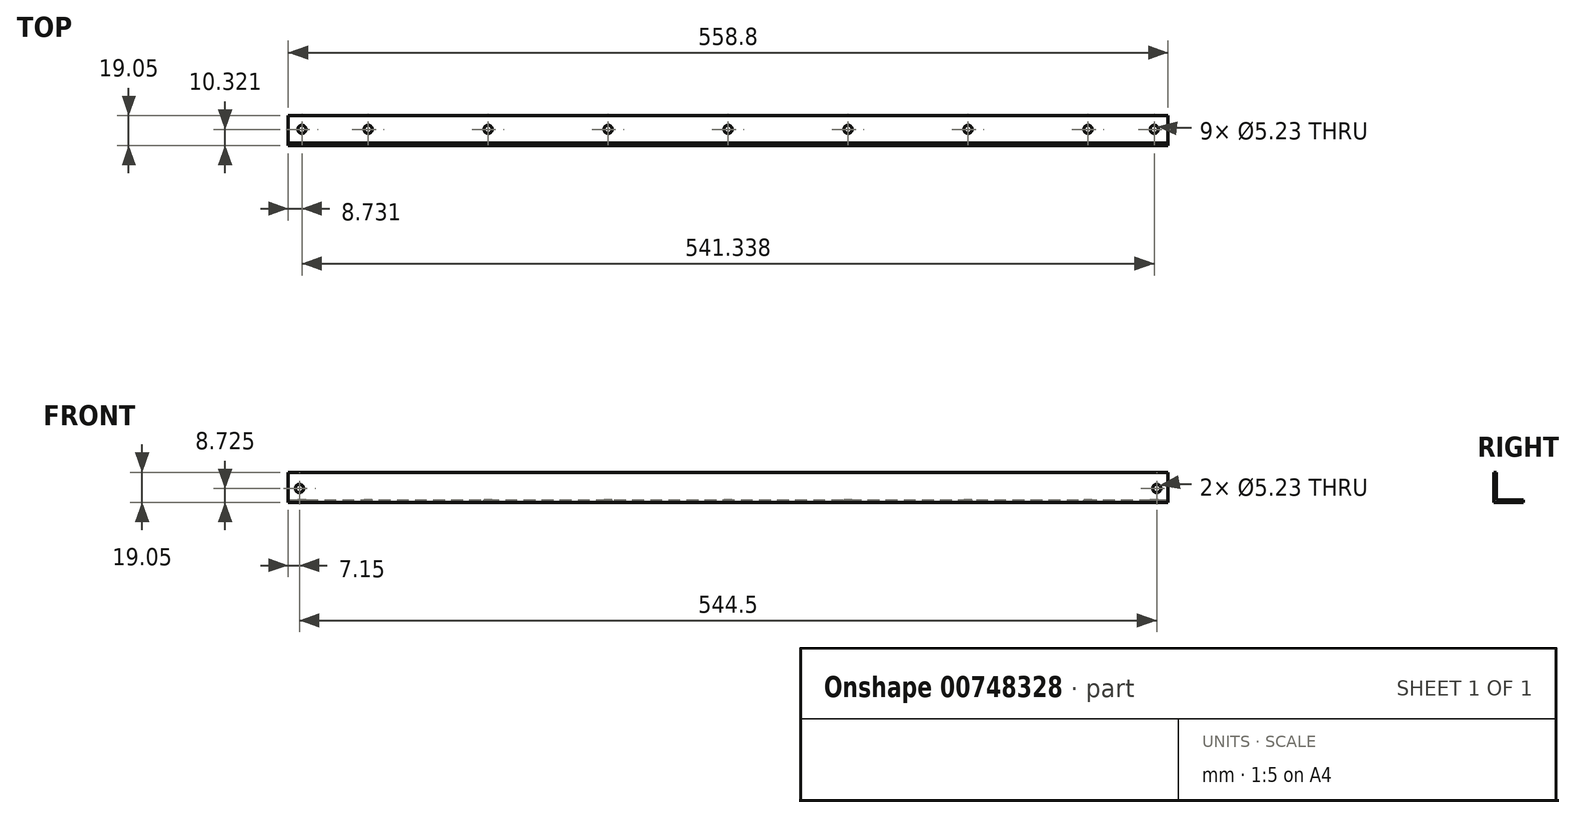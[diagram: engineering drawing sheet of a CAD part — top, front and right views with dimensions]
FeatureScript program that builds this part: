
annotation { "Feature Type Name" : "Feature", "Feature Type Description" : "" }
export const myFeature = defineFeature(function(context is Context, id is Id, definition is map)
    precondition{}
    {
        {
            var Q0;
            Q0=qCreatedBy(makeId("Right.planeOp"),FACE);
            var sketch = newSketch(context, id + "F0", { "sketchPlane" : qUnion([Q0])});
            skLineSegment(sketch, "E0", {"start": v(0, 0) * mm, "end": v(0, -17.46) * mm});
            skLineSegment(sketch, "E1", {"start": v(0, -17.46) * mm, "end": v(17.46, -17.46) * mm});
            skLineSegment(sketch, "E2.0", {"start": v(-1.59, -19.05) * mm, "end": v(17.46, -19.05) * mm});
            skLineSegment(sketch, "E2.1", {"start": v(-1.59, 0) * mm, "end": v(-1.59, -19.05) * mm});
            skLineSegment(sketch, "E3", {"start": v(-1.59, 0) * mm, "end": v(0, 0) * mm});
            skLineSegment(sketch, "E4", {"start": v(17.46, -17.46) * mm, "end": v(17.46, -19.05) * mm});
            skSolve(sketch);
        }
        {
            var Q0;
            Q0=makeQuery(id+"F0.imprint","IMPRINT",FACE,{"disambiguationData":[TD([[makeQuery(id+"F0.imprint","IMPRINT",EDGE,{"derivedFrom":sQuery(id+"F0.wireOp",EDGE,"E0")}),-1.0]])]});
            extrude(context, id + "F1", {"entities" : qUnion([Q0]), "oppositeDirection" : true, "depth" : 558.8 * mm, "offsetDistance" : 25.4 * mm});
        }
        {
            var Q0;
            Q0=makeQuery(id+"F1.opExtrude","SWEPT_FACE",FACE,{"disambiguationData":[OSD([sQuery(id+"F0.wireOp",EDGE,"E0")])]});
            var sketch = newSketch(context, id + "F2", { "sketchPlane" : qUnion([Q0])});
            skLineSegment(sketch, "E5.bottom", {"start": v(0, 0) * mm, "end": v(7.15, 0) * mm, "construction": true});
            skLineSegment(sketch, "E5.top", {"start": v(0, -17.46) * mm, "end": v(7.15, -17.46) * mm, "construction": true});
            skLineSegment(sketch, "E5.left", {"start": v(0, 0) * mm, "end": v(0, -17.46) * mm, "construction": true});
            skLineSegment(sketch, "E5.right", {"start": v(7.15, 0) * mm, "end": v(7.15, -17.46) * mm, "construction": true});
            skLineSegment(sketch, "E6.bottom", {"start": v(558.8, 0) * mm, "end": v(551.65, 0) * mm, "construction": true});
            skLineSegment(sketch, "E6.top", {"start": v(558.8, -17.46) * mm, "end": v(551.65, -17.46) * mm, "construction": true});
            skLineSegment(sketch, "E6.left", {"start": v(558.8, 0) * mm, "end": v(558.8, -17.46) * mm, "construction": true});
            skLineSegment(sketch, "E6.right", {"start": v(551.65, 0) * mm, "end": v(551.65, -17.46) * mm, "construction": true});
            skLineSegment(sketch, "E7.bottom", {"start": v(7.15, 0) * mm, "end": v(551.65, 0) * mm, "construction": true});
            skLineSegment(sketch, "E7.top", {"start": v(7.15, -17.46) * mm, "end": v(551.65, -17.46) * mm, "construction": true});
            skLineSegment(sketch, "E8.bottom", {"start": v(7.15, 0) * mm, "end": v(279.4, 0) * mm, "construction": true});
            skLineSegment(sketch, "E8.top", {"start": v(7.15, -17.46) * mm, "end": v(279.4, -17.46) * mm, "construction": true});
            skLineSegment(sketch, "E8.right", {"start": v(279.4, 0) * mm, "end": v(279.4, -17.46) * mm, "construction": true});
            skLineSegment(sketch, "E9.bottom", {"start": v(279.4, 0) * mm, "end": v(551.65, 0) * mm, "construction": true});
            skLineSegment(sketch, "E9.top", {"start": v(279.4, -17.46) * mm, "end": v(551.65, -17.46) * mm, "construction": true});
            skLineSegment(sketch, "E10.bottom", {"start": v(7.15, 0) * mm, "end": v(143.28, 0) * mm, "construction": true});
            skLineSegment(sketch, "E10.top", {"start": v(7.15, -17.46) * mm, "end": v(143.28, -17.46) * mm, "construction": true});
            skLineSegment(sketch, "E10.right", {"start": v(143.28, 0) * mm, "end": v(143.28, -17.46) * mm, "construction": true});
            skLineSegment(sketch, "E11.bottom", {"start": v(279.4, 0) * mm, "end": v(415.52, 0) * mm, "construction": true});
            skLineSegment(sketch, "E11.top", {"start": v(279.4, -17.46) * mm, "end": v(415.52, -17.46) * mm, "construction": true});
            skLineSegment(sketch, "E11.right", {"start": v(415.52, 0) * mm, "end": v(415.52, -17.46) * mm, "construction": true});
            skCircle(sketch, "E12", {"center": v(7.15, -10.33) * mm, "radius": 2.62 * mm});
            skCircle(sketch, "E13", {"center": v(551.65, -10.33) * mm, "radius": 2.62 * mm});
            skLineSegment(sketch, "E14", {"start": v(0, -10.33) * mm, "end": v(558.8, -10.33) * mm, "construction": true});
            skSolve(sketch);
        }
        {
            var Q0;
            Q0=makeQuery(id+"F1.opExtrude","SWEPT_FACE",FACE,{"disambiguationData":[OSD([sQuery(id+"F0.wireOp",EDGE,"E1")])]});
            var sketch = newSketch(context, id + "F3", { "sketchPlane" : qUnion([Q0])});
            skLineSegment(sketch, "E15", {"start": v(0, 8.73) * mm, "end": v(-558.8, 8.73) * mm, "construction": true});
            skLineSegment(sketch, "E16.bottom", {"start": v(0, 0) * mm, "end": v(-8.73, 0) * mm, "construction": true});
            skLineSegment(sketch, "E16.top", {"start": v(0, 17.46) * mm, "end": v(-8.73, 17.46) * mm, "construction": true});
            skLineSegment(sketch, "E16.left", {"start": v(0, 0) * mm, "end": v(0, 17.46) * mm, "construction": true});
            skLineSegment(sketch, "E16.right", {"start": v(-8.73, 0) * mm, "end": v(-8.73, 17.46) * mm, "construction": true});
            skLineSegment(sketch, "E17.bottom", {"start": v(-558.8, 0) * mm, "end": v(-550.07, 0) * mm, "construction": true});
            skLineSegment(sketch, "E17.top", {"start": v(-558.8, 17.46) * mm, "end": v(-550.07, 17.46) * mm, "construction": true});
            skLineSegment(sketch, "E17.left", {"start": v(-558.8, 0) * mm, "end": v(-558.8, 17.46) * mm, "construction": true});
            skLineSegment(sketch, "E17.right", {"start": v(-550.07, 0) * mm, "end": v(-550.07, 17.46) * mm, "construction": true});
            skCircle(sketch, "E18", {"center": v(-8.73, 8.73) * mm, "radius": 2.62 * mm});
            skCircle(sketch, "E19", {"center": v(-550.07, 8.73) * mm, "radius": 2.62 * mm});
            skLineSegment(sketch, "E20", {"start": v(-279.4, 17.46) * mm, "end": v(-279.4, 0) * mm, "construction": true});
            skLineSegment(sketch, "E21.1.0.0", {"start": v(-203.2, 17.46) * mm, "end": v(-203.2, 0) * mm, "construction": true});
            skLineSegment(sketch, "E21.2.0.0", {"start": v(-127, 17.46) * mm, "end": v(-127, 0) * mm, "construction": true});
            skLineSegment(sketch, "E21.3.0.0", {"start": v(-50.8, 17.46) * mm, "end": v(-50.8, 0) * mm, "construction": true});
            skLineSegment(sketch, "E21.direction1", {"start": v(-279.4, 0) * mm, "end": v(-203.2, 0) * mm, "construction": true});
            skLineSegment(sketch, "E22.1.0.0", {"start": v(-355.6, 17.46) * mm, "end": v(-355.6, 0) * mm, "construction": true});
            skLineSegment(sketch, "E22.2.0.0", {"start": v(-431.8, 17.46) * mm, "end": v(-431.8, 0) * mm, "construction": true});
            skLineSegment(sketch, "E22.3.0.0", {"start": v(-508, 17.46) * mm, "end": v(-508, 0) * mm, "construction": true});
            skLineSegment(sketch, "E22.direction1", {"start": v(-279.4, 0) * mm, "end": v(-355.6, 0) * mm, "construction": true});
            skCircle(sketch, "E23", {"center": v(-50.8, 8.73) * mm, "radius": 2.62 * mm});
            skCircle(sketch, "E24.1.0.0", {"center": v(-127, 8.73) * mm, "radius": 2.62 * mm});
            skCircle(sketch, "E24.2.0.0", {"center": v(-203.2, 8.73) * mm, "radius": 2.62 * mm});
            skCircle(sketch, "E24.3.0.0", {"center": v(-279.4, 8.73) * mm, "radius": 2.62 * mm});
            skCircle(sketch, "E24.4.0.0", {"center": v(-355.6, 8.73) * mm, "radius": 2.62 * mm});
            skCircle(sketch, "E24.5.0.0", {"center": v(-431.8, 8.73) * mm, "radius": 2.62 * mm});
            skCircle(sketch, "E24.6.0.0", {"center": v(-508, 8.73) * mm, "radius": 2.62 * mm});
            skLineSegment(sketch, "E24.direction1", {"start": v(-50.8, 8.73) * mm, "end": v(-127, 8.73) * mm, "construction": true});
            skSolve(sketch);
        }
        {
            var Q0;
            Q0 = qSketchRegion(id + "F2", true);
            extrude(context, id + "F4", {"entities" : qUnion([Q0]), "operationType" : NewBodyOperationType.REMOVE, "oppositeDirection" : true, "depth" : 25.4 * mm, "offsetDistance" : 25.4 * mm});
        }
        {
            var Q0;
            Q0 = qSketchRegion(id + "F3", true);
            extrude(context, id + "F5", {"entities" : qUnion([Q0]), "operationType" : NewBodyOperationType.REMOVE, "oppositeDirection" : true, "depth" : 25.4 * mm, "offsetDistance" : 25.4 * mm});
        }
    });
